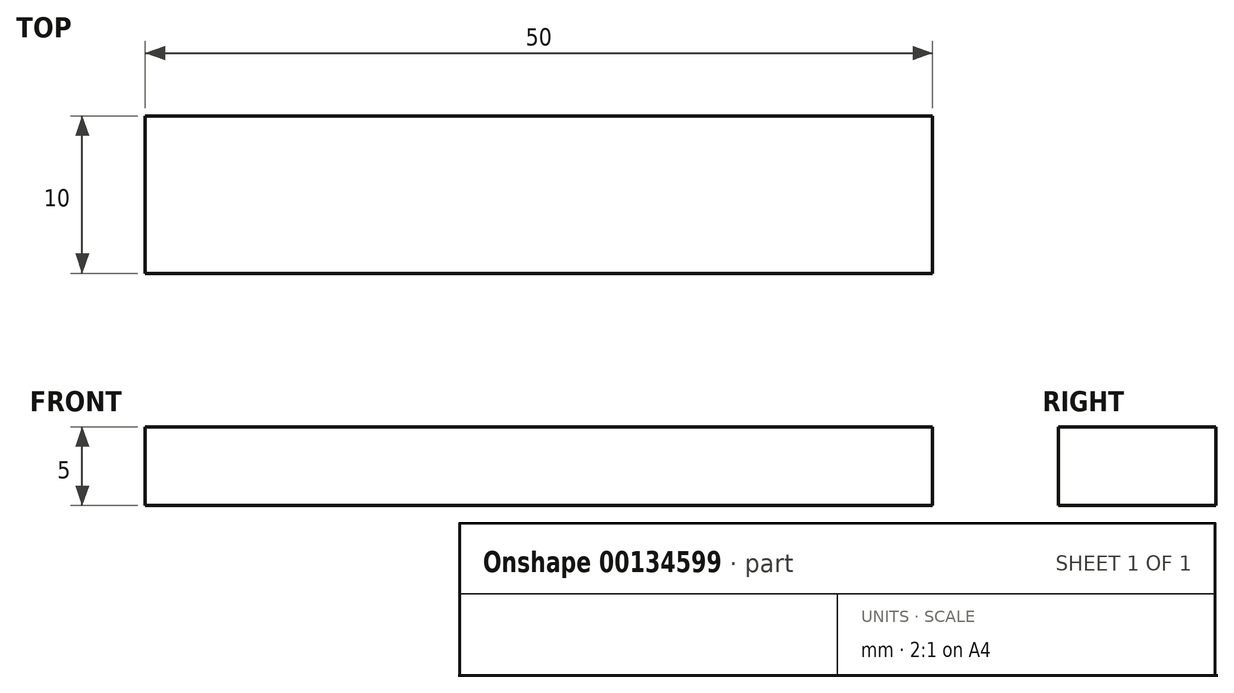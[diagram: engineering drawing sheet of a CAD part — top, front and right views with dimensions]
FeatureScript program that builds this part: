
annotation { "Feature Type Name" : "Feature", "Feature Type Description" : "" }
export const myFeature = defineFeature(function(context is Context, id is Id, definition is map)
    precondition{}
    {
        {
            var Q0;
            Q0=qCreatedBy(makeId("Top.planeOp"),FACE);
            var sketch = newSketch(context, id + "F0", { "sketchPlane" : qUnion([Q0])});
            skLineSegment(sketch, "E0.bottom", {"start": v(-23.8, -3.49) * mm, "end": v(26.2, -3.49) * mm});
            skLineSegment(sketch, "E0.top", {"start": v(-23.8, -13.49) * mm, "end": v(26.2, -13.49) * mm});
            skLineSegment(sketch, "E0.left", {"start": v(-23.8, -3.49) * mm, "end": v(-23.8, -13.49) * mm});
            skLineSegment(sketch, "E0.right", {"start": v(26.2, -3.49) * mm, "end": v(26.2, -13.49) * mm});
            skSolve(sketch);
        }
        {
            var Q0;
            Q0=makeQuery(id+"F0.imprint","IMPRINT",FACE,{"disambiguationData":[TD([[makeQuery(id+"F0.imprint","IMPRINT",EDGE,{"derivedFrom":sQuery(id+"F0.wireOp",EDGE,"E0.bottom")}),-1.0]])]});
            extrude(context, id + "F1", {"entities" : qUnion([Q0]), "depth" : 5 * mm});
        }
    });
